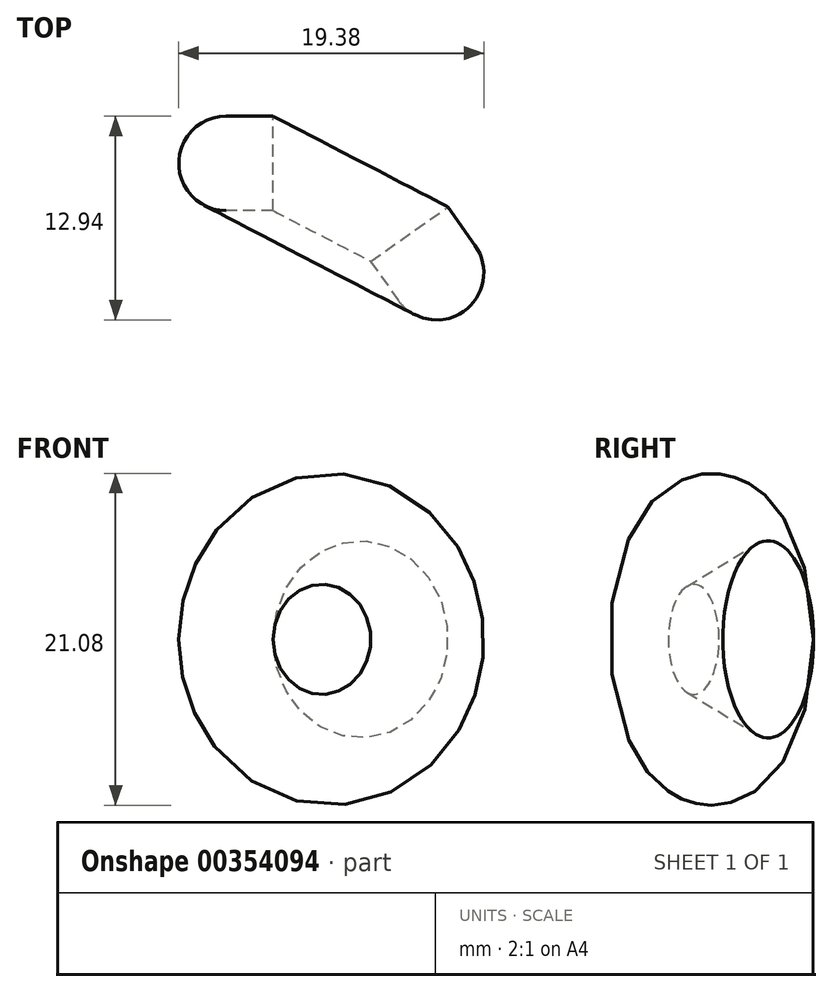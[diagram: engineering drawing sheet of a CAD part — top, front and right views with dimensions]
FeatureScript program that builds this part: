
annotation { "Feature Type Name" : "Feature", "Feature Type Description" : "" }
export const myFeature = defineFeature(function(context is Context, id is Id, definition is map)
    precondition{}
    {
        {
            var Q0;
            Q0=qCreatedBy(makeId("Top.planeOp"),FACE);
            var sketch = newSketch(context, id + "F0", { "sketchPlane" : qUnion([Q0])});
            skLineSegment(sketch, "E0", {"start": v(0, 0) * mm, "end": v(0, 6) * mm});
            skLineSegment(sketch, "E1", {"start": v(0, 6) * mm, "end": v(-3, 6) * mm});
            skLineSegment(sketch, "E2", {"start": v(-3, 6) * mm, "end": v(-3, 0) * mm});
            skLineSegment(sketch, "E3", {"start": v(-3, 0) * mm, "end": v(0, 0) * mm});
            skArc(sketch, "E4", {"start": v(-3, 6) * mm, "mid": v(-6, 3) * mm, "end": v(-3, 0) * mm});
            skPoint(sketch, "E5.visualSharp", {"position": v(-3, 6) * mm});
            skLineSegment(sketch, "E5.filletArc", {"start": v(-3, 6) * mm, "end": v(-3, 6) * mm});
            skLineSegment(sketch, "E6", {"start": v(7, 5.9) * mm, "end": v(3.93, 0) * mm});
            skSolve(sketch);
        }
        {
            var Q0;
            Q0=makeQuery(id+"F0.imprint","IMPRINT",FACE,{"disambiguationData":[TD([[makeQuery(id+"F0.imprint","IMPRINT",EDGE,{"derivedFrom":sQuery(id+"F0.wireOp",EDGE,"E2")}),-1.0]])]});
            var Q1;
            Q1=makeQuery(id+"F0.imprint","IMPRINT",FACE,{"disambiguationData":[TD([[makeQuery(id+"F0.imprint","IMPRINT",EDGE,{"derivedFrom":sQuery(id+"F0.wireOp",EDGE,"E0")}),1.0]])]});
            var Q2;
            Q2=sQuery(id+"F0.wireOp",EDGE,"E6");
            revolve(context, id + "F1", {"entities" : qUnion([Q0, Q1]), "axis" : qUnion([Q2]), "revolveType" : RevolveType.FULL});
        }
    });
